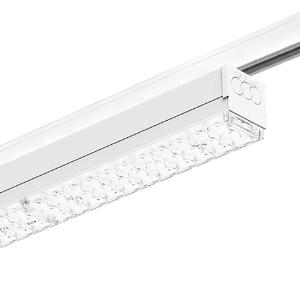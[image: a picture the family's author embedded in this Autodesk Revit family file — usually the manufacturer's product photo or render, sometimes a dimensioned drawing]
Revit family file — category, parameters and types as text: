
# Revit family: 3f_filippi_-_3f_zeta_track_l_ampio_3f_filippi_-_47124_-_3f_zeta_tk_l_50_ampio_l1783
name_source: partatom
category: Lighting Fixtures
units: mm (PartAtom-declared; Revit-internal decimal feet)

## family parameters
Cut with Voids When Loaded = No
Host = Face
Light Source = No
Part Type = Normal
Room Calculation Point = No
Round Connector Dimension = Use Diameter
Shared = No

## types (1)
- 3F Filippi - 3F Zeta Track L Ampio (1 x LED, 8247 lm, 46 W, 4000 K)
    Apparent Load = 46 VA
    Approval mark = CE
    CIE Flux Codes = 61 95 99 99 100
    Color Rendering = 80
    Color Temperature = 4000 K
    Control Gear = Electronic ballast
    Default Elevation = 1800 mm
    Description = ILLUMINOTECHNICAL
Luminous efficiency 100% (DLOR 99%, ULOR 1%).
Initial luminous flux of the luminaire 8247 lm.
Symmetric wide direct distribution.
Installation Interdistance Transv.D = 1.39 x hu - Long.D = 1.43 x hu.
Tabular UGR (CIE 117 - 4H-8H; S=0.25H; 70/50/20): RUG 21.7 - 22.4.
Beam angle: 102° - 103°.
Luminous efficacy 179 lm/W.
Lifetime (L93/B10): 30000 h. (tq+25°C)
Lifetime (L90/B10): 50000 h. (tq+25°C)
Lifetime (L85/B10): 80000 h. (tq+25°C)
Lifetime (L80/B10): 100000 h. (tq+25°C)
Sudden decreased luminous flux after 50000 hours: 0% (C0).
Photobiological safety in compliance with IEC/TR 62778: RG0 risk exempt, (IEC 62471).
In compliance with IEC/EN 62722-2-1 - IEC/EN 62717 standards.

SOURCE
Linear LED module 50W/840.
Energy efficiency class (UE 2019/2020 - UE 2019/2015): C.
CIE 13.3 Colour rendering index: CRI >80 (R9 <50%).
IES TM-30 Fidelity Index: Rf = 84 Rg = 95.
CCT nominal colour temperature 4000 K.
Colour initial tolerance (MacAdam): SDCM 3.

MECHANICAL
Housing in hot-galvanised steel, painted in white polyester, obtained through rolling process with adapters to busbar in white polycarbonate.
Mechanical truck adapter.
Light unit in hot-galvanised steel, painted in white polyester base with fixing springs and retractable safety hooks in stainless steel.
Lenses for wide distribution, in transparent methacrylate (PMMA) with external flat surface.
End caps in white polycarbonate.
Luminaire with limited surface temperature. - D - (EN 60598-2-24)
Dimensions: 1783x62 mm, height 67 mm. Weight 3.835 kg.
IP40 protection degree.
Mechanical strength to impacts IK06 (1 joule).
Glow-wire test resistance 650°C.

ELECTRICAL
Halogen Free electronic wiring 230V-50/60Hz, power factor 0.95, THD <25%, constant output current, class I, 1 driver.
Power of the luminaire 46 W.
ENEC - CE.
SAFE FLICKER: PstLM=<1 and SVM=<0.4 (IEC TR 61547-1 and IEC TR 63158), to ensure a more comfortable and safe light.
Ambient temperature from 0°C to +25°C.
Temperature class T6 max 85°C.
Truck adapter, 4-way.
Relative humidity UR: <85%.

INSTALLATION
Track.
This product is suitable for installation on a 3-phase electrified busbar "Binario 3F".

APPLICATIONS
Environments: architectural, commercial, transit areas, cornices, boards.

WARNING
Luminaire designed for disposal/recycling at end-of-life.
Replaceable (LED only) light source by a professional. Replaceable control gear by a professional.
    Height = 67 mm
    Lamp = 1 x LED
    Lamp Light Flux = 8247 lm
    Lamp Power = 46 W
    Lamp count = 1
    Length = 1783 mm
    Lifetime = 50000 h
    Luminous efficacy = 179 lm/W
    Manufacturer = 3F Filippi
    ModVariant = No
    Model = 3F Filippi - 47124 - 3F Zeta TK L 50 AMPIO L1783
    Mounting Place = Ceiling
    Mounting Type = Rail mounted
    Number of Poles = 1
    OnlyDefault = Yes
    Power Factor = 1
    Product Name = 3F Filippi - 3F Zeta Track L Ampio
    Product group = track mounted spotlight
    ProductGroupID = 12
    Protection Class = Protection class I
    Protection Degree = IP 40
    RLX_Detail_Level = 1
    RLX_Emergency_Light_Flux = 0 lm
    RLX_Emergency_Type = 0
    RLX_Emergency_Type_DB = No
    RlxData = <blob elided: 132101 chars, md5=3c11daf0>
    Socket = socket
    Standby Power = 0 W
    System Light Flux = 8247 lm
    System Power = 46 W
    Type Comments = Product without accessories
    Type Image = 3ffilippi_3f_zeta_track_l_ampio.jpg
    URL = http://relux.com
    VarID = ---
    Voltage = 0 V
    Weight = 0.00 kg
    Width = 62 mm  [stored 0.203412 ft]

note: [stored X ft] marks values corroborated as IEEE doubles in the binary element streams (Revit-internal decimal feet)

## geometry (parser evidence)
native form markers: Blend x4, Sweep x10
no freeform markers — native parametric forms only
